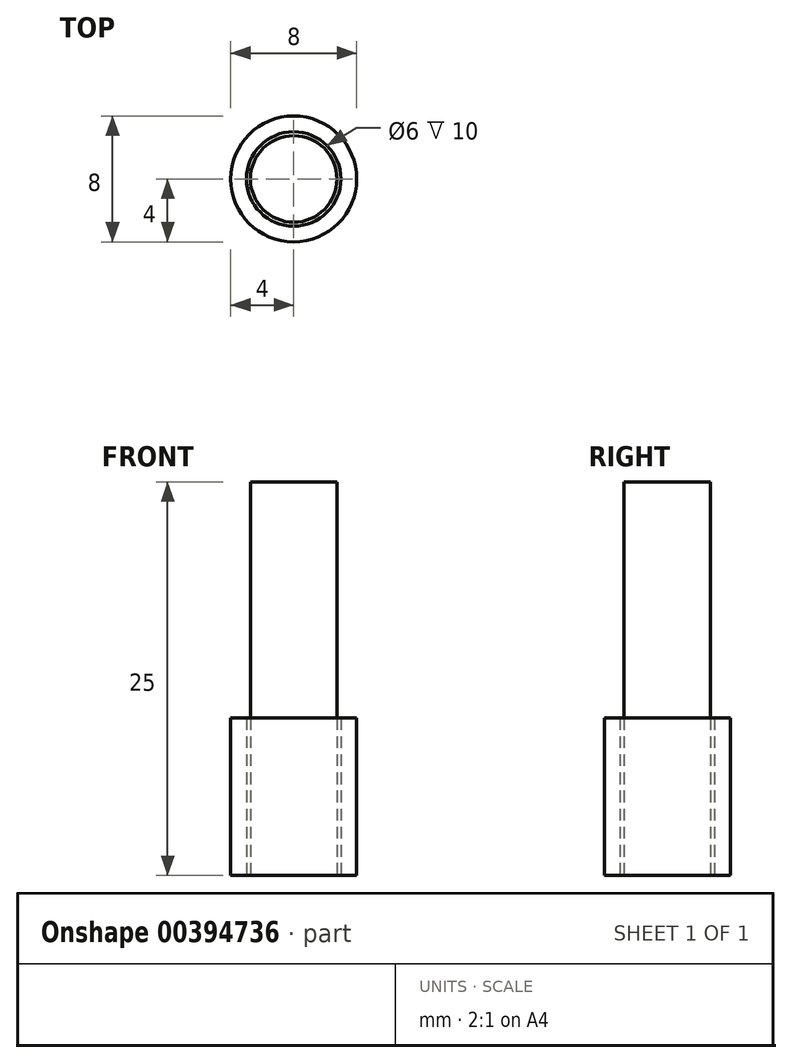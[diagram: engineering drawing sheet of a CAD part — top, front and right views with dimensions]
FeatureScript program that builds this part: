
annotation { "Feature Type Name" : "Feature", "Feature Type Description" : "" }
export const myFeature = defineFeature(function(context is Context, id is Id, definition is map)
    precondition{}
    {
        {
            var Q0;
            Q0=qCreatedBy(makeId("Top.planeOp"),FACE);
            var sketch = newSketch(context, id + "F0", { "sketchPlane" : qUnion([Q0])});
            skCircle(sketch, "E0", {"center": v(0, 0) * mm, "radius": 4 * mm});
            skCircle(sketch, "E1", {"center": v(0, 0) * mm, "radius": 3 * mm});
            skSolve(sketch);
        }
        {
            var Q0;
            Q0=makeQuery(id+"F0.imprint","IMPRINT",FACE,{"disambiguationData":[TD([[makeQuery(id+"F0.imprint","IMPRINT",EDGE,{"derivedFrom":sQuery(id+"F0.wireOp",EDGE,"E0")}),1.0]])]});
            extrude(context, id + "F1", {"entities" : qUnion([Q0]), "depth" : 10 * mm});
        }
        {
            var Q0;
            Q0=makeQuery(id+"F0.imprint","IMPRINT",FACE,{"disambiguationData":[TD([[makeQuery(id+"F0.imprint","IMPRINT",EDGE,{"derivedFrom":sQuery(id+"F0.wireOp",EDGE,"E1")}),1.0]])]});
            var sketch = newSketch(context, id + "F2", { "sketchPlane" : qUnion([Q0])});
            skCircle(sketch, "E2", {"center": v(0, 0) * mm, "radius": 2.75 * mm});
            skSolve(sketch);
        }
        {
            var Q0;
            Q0=makeQuery(id+"F2.imprint","IMPRINT",FACE,{"disambiguationData":[TD([[makeQuery(id+"F2.imprint","IMPRINT",EDGE,{"derivedFrom":sQuery(id+"F2.wireOp",EDGE,"E2")}),1.0]])]});
            extrude(context, id + "F3", {"entities" : qUnion([Q0]), "depth" : 25 * mm});
        }
    });
